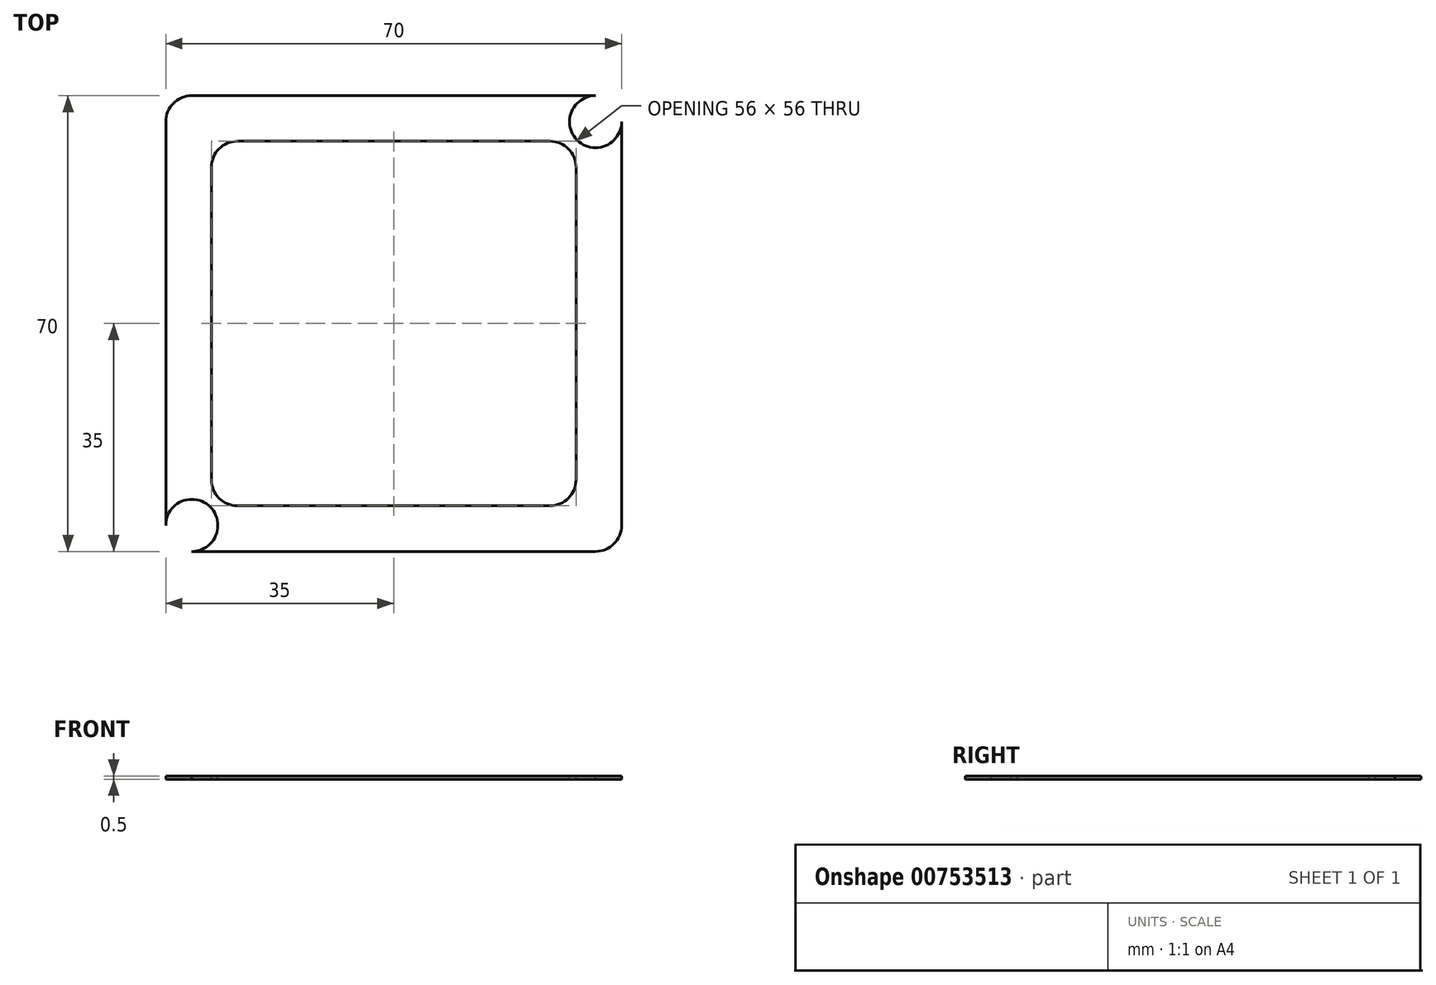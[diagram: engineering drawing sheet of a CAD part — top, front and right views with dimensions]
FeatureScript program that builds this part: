
annotation { "Feature Type Name" : "Feature", "Feature Type Description" : "" }
export const myFeature = defineFeature(function(context is Context, id is Id, definition is map)
    precondition{}
    {
        {
            var Q0;
            Q0=qCreatedBy(makeId("Top.planeOp"),FACE);
            var sketch = newSketch(context, id + "F0", { "sketchPlane" : qUnion([Q0])});
            skLineSegment(sketch, "E0.bottom", {"start": v(-31, 35) * mm, "end": v(31, 35) * mm});
            skLineSegment(sketch, "E0.top", {"start": v(-31, -35) * mm, "end": v(31, -35) * mm});
            skLineSegment(sketch, "E0.left", {"start": v(-35, 31) * mm, "end": v(-35, -31) * mm});
            skLineSegment(sketch, "E0.right", {"start": v(35, 31) * mm, "end": v(35, -31) * mm});
            skPoint(sketch, "E0.middle", {"position": v(0, 0) * mm});
            skLineSegment(sketch, "E1.0", {"start": v(-28, 28) * mm, "end": v(28, 28) * mm});
            skLineSegment(sketch, "E1.1", {"start": v(-28, 28) * mm, "end": v(-28, -28) * mm});
            skLineSegment(sketch, "E1.2", {"start": v(-28, -28) * mm, "end": v(28, -28) * mm});
            skLineSegment(sketch, "E1.3", {"start": v(28, 28) * mm, "end": v(28, -28) * mm});
            skCircle(sketch, "E2", {"center": v(-31, 31) * mm, "radius": 4 * mm});
            skCircle(sketch, "E3.MirrorC", {"center": v(31, 31) * mm, "radius": 4 * mm});
            skCircle(sketch, "E4.MirrorC", {"center": v(31, -31) * mm, "radius": 4 * mm});
            skCircle(sketch, "E5.MirrorC", {"center": v(-31, -31) * mm, "radius": 4 * mm});
            skPoint(sketch, "E6.orphan", {"position": v(35, 35) * mm});
            skPoint(sketch, "E7.orphan", {"position": v(35, -35) * mm});
            skPoint(sketch, "E8.orphan", {"position": v(-35, -35) * mm});
            skLineSegment(sketch, "E9.0", {"start": v(-27.54, -33) * mm, "end": v(27.54, -33) * mm});
            skLineSegment(sketch, "E9.1", {"start": v(-33, 27.54) * mm, "end": v(-33, -27.54) * mm});
            skLineSegment(sketch, "E9.2", {"start": v(-27.54, 33) * mm, "end": v(27.54, 33) * mm});
            skLineSegment(sketch, "E9.3", {"start": v(33, 27.54) * mm, "end": v(33, -27.54) * mm});
            skLineSegment(sketch, "E10", {"start": v(-35, -35) * mm, "end": v(-28, -28) * mm, "construction": true});
            skCircle(sketch, "E11", {"center": v(-32.3, -32.3) * mm, "radius": 2.15 * mm, "construction": true});
            skCircle(sketch, "E12.MirrorC", {"center": v(32.3, -32.3) * mm, "radius": 2.15 * mm, "construction": true});
            skCircle(sketch, "E13.MirrorC", {"center": v(32.3, 32.3) * mm, "radius": 2.15 * mm, "construction": true});
            skCircle(sketch, "E14.MirrorC", {"center": v(-32.3, 32.3) * mm, "radius": 2.15 * mm, "construction": true});
            skPoint(sketch, "E15", {"position": v(32.9, 32.3) * mm});
            skPoint(sketch, "E16", {"position": v(32.9, -31.7) * mm});
            skPoint(sketch, "E17", {"position": v(-32.3, -31.7) * mm});
            skSolve(sketch);
        }
        {
            var Q0;
            Q0=makeQuery(id+"F0.imprint","IMPRINT",FACE,{"disambiguationData":[TD([[makeQuery(id+"F0.imprint","IMPRINT",EDGE,{"derivedFrom":sQuery(id+"F0.wireOp",EDGE,"E1.0")}),1.0]])]});
            var Q1;
            {var subQ0=sQuery(id+"F0.wireOp",EDGE,"E0.bottom");Q1=makeQuery(id+"F0.imprint","IMPRINT",FACE,{"disambiguationData":[TD([[makeQuery(id+"F0.imprint","IMPRINT",EDGE,{"derivedFrom":subQ0}),-1.0]])]});}
            var Q2;
            {var subQ0=sQuery(id+"F0.wireOp",EDGE,"E3.MirrorC");var subQ1=makeQuery(id+"F0.imprint","INTERSECT",VERTEX,{"derivedFrom":[sQuery(id+"F0.wireOp",EDGE,"E0.bottom"),subQ0]});Q2=makeQuery(id+"F0.imprint","IMPRINT",FACE,{"disambiguationData":[TD([[makeQuery(id+"F0.imprint","IMPRINT",EDGE,{"disambiguationData":[TD([[subQ1,1.0]])],"derivedFrom":subQ0}),-1.0]])]});}
            var Q3;
            {var subQ0=sQuery(id+"F0.wireOp",EDGE,"E0.right");Q3=makeQuery(id+"F0.imprint","IMPRINT",FACE,{"disambiguationData":[TD([[makeQuery(id+"F0.imprint","IMPRINT",EDGE,{"derivedFrom":subQ0}),-1.0]])]});}
            var Q4;
            {var subQ0=sQuery(id+"F0.wireOp",EDGE,"E4.MirrorC");var subQ1=makeQuery(id+"F0.imprint","INTERSECT",VERTEX,{"derivedFrom":[sQuery(id+"F0.wireOp",EDGE,"E0.top"),subQ0]});Q4=makeQuery(id+"F0.imprint","IMPRINT",FACE,{"disambiguationData":[TD([[makeQuery(id+"F0.imprint","IMPRINT",EDGE,{"disambiguationData":[TD([[subQ1,1.0]])],"derivedFrom":subQ0}),1.0]])]});}
            var Q5;
            {var subQ0=sQuery(id+"F0.wireOp",EDGE,"E0.top");Q5=makeQuery(id+"F0.imprint","IMPRINT",FACE,{"disambiguationData":[TD([[makeQuery(id+"F0.imprint","IMPRINT",EDGE,{"derivedFrom":subQ0}),1.0]])]});}
            var Q6;
            {var subQ0=sQuery(id+"F0.wireOp",EDGE,"E0.left");Q6=makeQuery(id+"F0.imprint","IMPRINT",FACE,{"disambiguationData":[TD([[makeQuery(id+"F0.imprint","IMPRINT",EDGE,{"derivedFrom":subQ0}),1.0]])]});}
            var Q7;
            {var subQ0=sQuery(id+"F0.wireOp",EDGE,"E5.MirrorC");var subQ1=makeQuery(id+"F0.imprint","INTERSECT",VERTEX,{"derivedFrom":[sQuery(id+"F0.wireOp",EDGE,"E0.top"),subQ0]});Q7=makeQuery(id+"F0.imprint","IMPRINT",FACE,{"disambiguationData":[TD([[makeQuery(id+"F0.imprint","IMPRINT",EDGE,{"disambiguationData":[TD([[subQ1,1.0]])],"derivedFrom":subQ0}),-1.0]])]});}
            var Q8;
            {var subQ0=sQuery(id+"F0.wireOp",EDGE,"E2");var subQ1=makeQuery(id+"F0.imprint","INTERSECT",VERTEX,{"derivedFrom":[sQuery(id+"F0.wireOp",EDGE,"E0.bottom"),subQ0]});Q8=makeQuery(id+"F0.imprint","IMPRINT",FACE,{"disambiguationData":[TD([[makeQuery(id+"F0.imprint","IMPRINT",EDGE,{"disambiguationData":[TD([[subQ1,1.0]])],"derivedFrom":subQ0}),1.0]])]});}
            extrude(context, id + "F1", {"entities" : qUnion([Q0, Q1, Q2, Q3, Q4, Q5, Q6, Q7, Q8]), "oppositeDirection" : true, "depth" : .5 * mm, "offsetDistance" : 25 * mm});
        }
        {
            var Q0;
            Q0=makeQuery(id+"F1.opExtrude","SWEPT_EDGE",EDGE,{"disambiguationData":[OSD([sQuery(id+"F0.wireOp",EDGE,"E1.1"),sQuery(id+"F0.wireOp",EDGE,"E1.2")])]});
            var Q1;
            Q1=makeQuery(id+"F1.opExtrude","SWEPT_EDGE",EDGE,{"disambiguationData":[OSD([sQuery(id+"F0.wireOp",EDGE,"E1.0"),sQuery(id+"F0.wireOp",EDGE,"E1.1")])]});
            var Q2;
            Q2=makeQuery(id+"F1.opExtrude","SWEPT_EDGE",EDGE,{"disambiguationData":[OSD([sQuery(id+"F0.wireOp",EDGE,"E1.0"),sQuery(id+"F0.wireOp",EDGE,"E1.3")])]});
            var Q3;
            Q3=makeQuery(id+"F1.opExtrude","SWEPT_EDGE",EDGE,{"disambiguationData":[OSD([sQuery(id+"F0.wireOp",EDGE,"E1.2"),sQuery(id+"F0.wireOp",EDGE,"E1.3")])]});
            fillet(context, id + "F2", {"entities" : qUnion([Q0, Q1, Q2, Q3]), "radius" : 4 * mm, "tangentPropagation" : true, "allowEdgeOverflow" : false});
        }
        {
            var Q0;
            Q0=qCreatedBy(makeId("Top.planeOp"),FACE);
            var sketch = newSketch(context, id + "F3", { "sketchPlane" : qUnion([Q0])});
            skLineSegment(sketch, "E18.bottom", {"start": v(-30, 30) * mm, "end": v(30, 30) * mm});
            skLineSegment(sketch, "E18.top", {"start": v(-30, -30) * mm, "end": v(30, -30) * mm});
            skLineSegment(sketch, "E18.left", {"start": v(-30, 30) * mm, "end": v(-30, -30) * mm});
            skLineSegment(sketch, "E18.right", {"start": v(30, 30) * mm, "end": v(30, -30) * mm});
            skPoint(sketch, "E18.middle", {"position": v(0, 0) * mm});
            skSolve(sketch);
        }
    });
